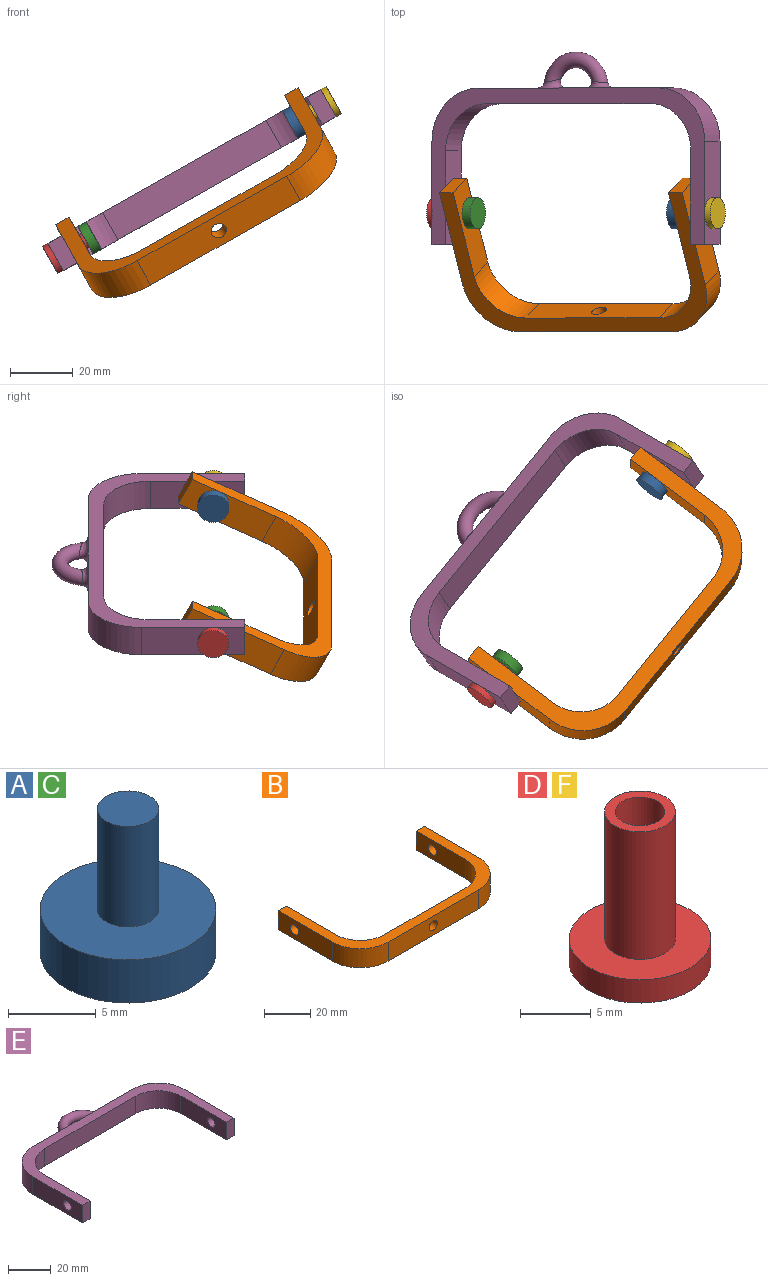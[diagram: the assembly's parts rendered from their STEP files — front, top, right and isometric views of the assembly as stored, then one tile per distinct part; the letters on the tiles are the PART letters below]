
ASSEMBLY  parts=6 mates=5
PART A: 5 faces, bbox 10x10x10 mm
  f0: cylinder r=1.75mm len=7mm, axis (0,0,-1), area 77mm2, adj f1,f3
  f1: plane 3.5x3.5mm, normal (0,0,1), area 9.6mm2, adj f0
  f2: cylinder r=5mm len=10mm, axis (0,0,-1), area 94.2mm2, adj f3,f4
  f3: plane 10x10mm, normal (0,0,1), area 68.9mm2, adj f0,f2
  f4: plane 10x10mm, normal (0,0,-1), area 78.5mm2, adj f2
PART B: 17 faces, bbox 89x50x10 mm
  f0: plane 10x5mm, normal (0,1,0), area 50mm2, adj f1,f7,f8,f9
  f1: plane 30x10mm, normal (-1,0,0), area 280.4mm2, adj f0,f8,f9,f10,f12
  f2: plane 49x10mm, normal (0,1,0), area 470.4mm2, adj f8,f9,f10,f11,f14
  f3: plane 30x10mm, normal (1,0,0), area 280.4mm2, adj f4,f8,f9,f11,f13
  f4: plane 10x5mm, normal (0,1,0), area 50mm2, adj f3,f5,f8,f9
  f5: plane 33x10mm, normal (-1,0,0), area 310.4mm2, adj f4,f8,f9,f13,f15
  f6: plane 55x10mm, normal (0,-1,0), area 530.4mm2, adj f8,f9,f14,f15,f16
  f7: plane 33x10mm, normal (1,0,0), area 310.4mm2, adj f0,f8,f9,f12,f16
  f8: plane 89x50mm, normal (0,0,1), area 867.5mm2, adj f0,f1,f2,f3,f4,f5,f6,f7
  f9: plane 89x50mm, normal (0,0,-1), area 867.5mm2, adj f0,f1,f2,f3,f4,f5,f6,f7
  f10: cylinder r=15mm len=15mm, axis (0,0,-1), area 235.6mm2, adj f1,f2,f8,f9
  f11: cylinder r=15mm len=15mm, axis (0,0,1), area 235.6mm2, adj f2,f3,f8,f9
  f12: cylinder r=2.5mm len=5mm, axis (-1,0,0), area 78.5mm2, adj f1,f7
  f13: cylinder r=2.5mm len=5mm, axis (-1,0,0), area 78.5mm2, adj f3,f5
  f14: cylinder r=2.5mm len=5mm, axis (0,-1,0), area 78.5mm2, adj f2,f6
  f15: cylinder r=17mm len=17mm, axis (0,0,-1), area 267mm2, adj f5,f6,f8,f9
  f16: cylinder r=17mm len=17mm, axis (0,0,1), area 267mm2, adj f6,f7,f8,f9
PART C: same geometry as A
PART D: 7 faces, bbox 10x10x13 mm
  f0: cylinder r=5mm len=10mm, axis (0,0,-1), area 62.8mm2, adj f1,f2
  f1: plane 10x10mm, normal (0,0,1), area 58.9mm2, adj f0,f3
  f2: plane 10x10mm, normal (0,0,-1), area 78.5mm2, adj f0
  f3: cylinder r=2.5mm len=11mm, axis (0,0,-1), area 172.8mm2, adj f1,f4
  f4: plane 5x5mm, normal (0,0,1), area 10mm2, adj f3,f5
  f5: cylinder r=1.75mm len=10mm, axis (0,0,1), area 110mm2, adj f4,f6
  f6: plane 3.5x3.5mm, normal (0,0,1), area 9.6mm2, adj f5
PART E: 19 faces, bbox 100x62.4x10 mm
  f0: plane 30x10mm, normal (-1,0,0), area 280.4mm2, adj f1,f8,f9,f11,f13
  f1: plane 10x5mm, normal (0,-1,0), area 50mm2, adj f0,f2,f8,f9
  f2: plane 33x10mm, normal (1,0,0), area 310.4mm2, adj f1,f8,f9,f13,f14
  f3: plane 66x10mm, normal (0,1,0), area 528.5mm2, adj f8,f9,f14,f15,f17,f18
  f4: plane 33x10mm, normal (-1,0,0), area 310.4mm2, adj f5,f8,f9,f12,f15
  f5: plane 10x5mm, normal (0,-1,0), area 50mm2, adj f4,f6,f8,f9
  f6: plane 30x10mm, normal (1,0,0), area 280.4mm2, adj f5,f8,f9,f10,f12
  f7: plane 60x10mm, normal (0,-1,0), area 600mm2, adj f8,f9,f10,f11
  f8: plane 100x50mm, normal (0,0,1), area 922.5mm2, adj f0,f1,f2,f3,f4,f5,f6,f7
  f9: plane 100x50mm, normal (0,0,-1), area 922.5mm2, adj f0,f1,f2,f3,f4,f5,f6,f7
  f10: cylinder r=15mm len=15mm, axis (0,0,-1), area 235.6mm2, adj f6,f7,f8,f9
  f11: cylinder r=15mm len=15mm, axis (0,0,1), area 235.6mm2, adj f0,f7,f8,f9
  f12: cylinder r=2.5mm len=5mm, axis (-1,0,0), area 78.5mm2, adj f4,f6
  f13: cylinder r=2.5mm len=5mm, axis (-1,0,0), area 78.5mm2, adj f0,f2
  f14: cylinder r=17mm len=17mm, axis (0,0,-1), area 267mm2, adj f2,f3,f8,f9
  f15: cylinder r=17mm len=17mm, axis (0,0,1), area 267mm2, adj f3,f4,f8,f9
  f16: torus R=9mm, axis (0,0,-1), area 376mm2, adj f17,f18
  f17: bspline ~9.33x9.01mm, area 67.5mm2, adj f3,f16
  f18: bspline ~9.33x9.01mm, area 67.5mm2, adj f3,f16
PART F: same geometry as D
PLACE A rot(axis=(0.45,0.45,0.77),104.7deg) t=(199.99,-39.05,-112.02)mm
PLACE B rot(axis=(-0.06,0.97,0.23),151.4deg) t=(169.38,-50.94,-132.04)mm
PLACE C rot(axis=(-0.65,-0.65,0.38),138.2deg) t=(137.3,-39.05,-147.42)mm
PLACE D rot(axis=(0.5,0,0.86),180deg) t=(123.36,-35.31,-155.28)mm
PLACE E rot(axis=(0,1,0),150.5deg) t=(166.19,-20.31,-125.36)mm fixed
PLACE F rot(axis=(0.86,0,-0.5),180deg) t=(213.93,-35.31,-104.15)mm
MATE fastened F.f3 <-> E.f12  axis (-0.87,0,-0.49) through (212.18,-35.31,-105.13)mm
MATE fastened A.f0 <-> F.f5  axis (0.87,0,0.49) through (202.61,-35.31,-110.54)mm
MATE fastened D.f0 <-> E.f12  axis (0.87,0,0.49) through (125.11,-35.31,-154.3)mm
MATE revolute E.f12 <-> B.f12  axis (0.87,0,0.49) through (129.46,-35.31,-151.84)mm
MATE fastened C.f0 <-> D.f3  axis (-0.87,0,-0.49) through (134.68,-35.31,-148.89)mm
